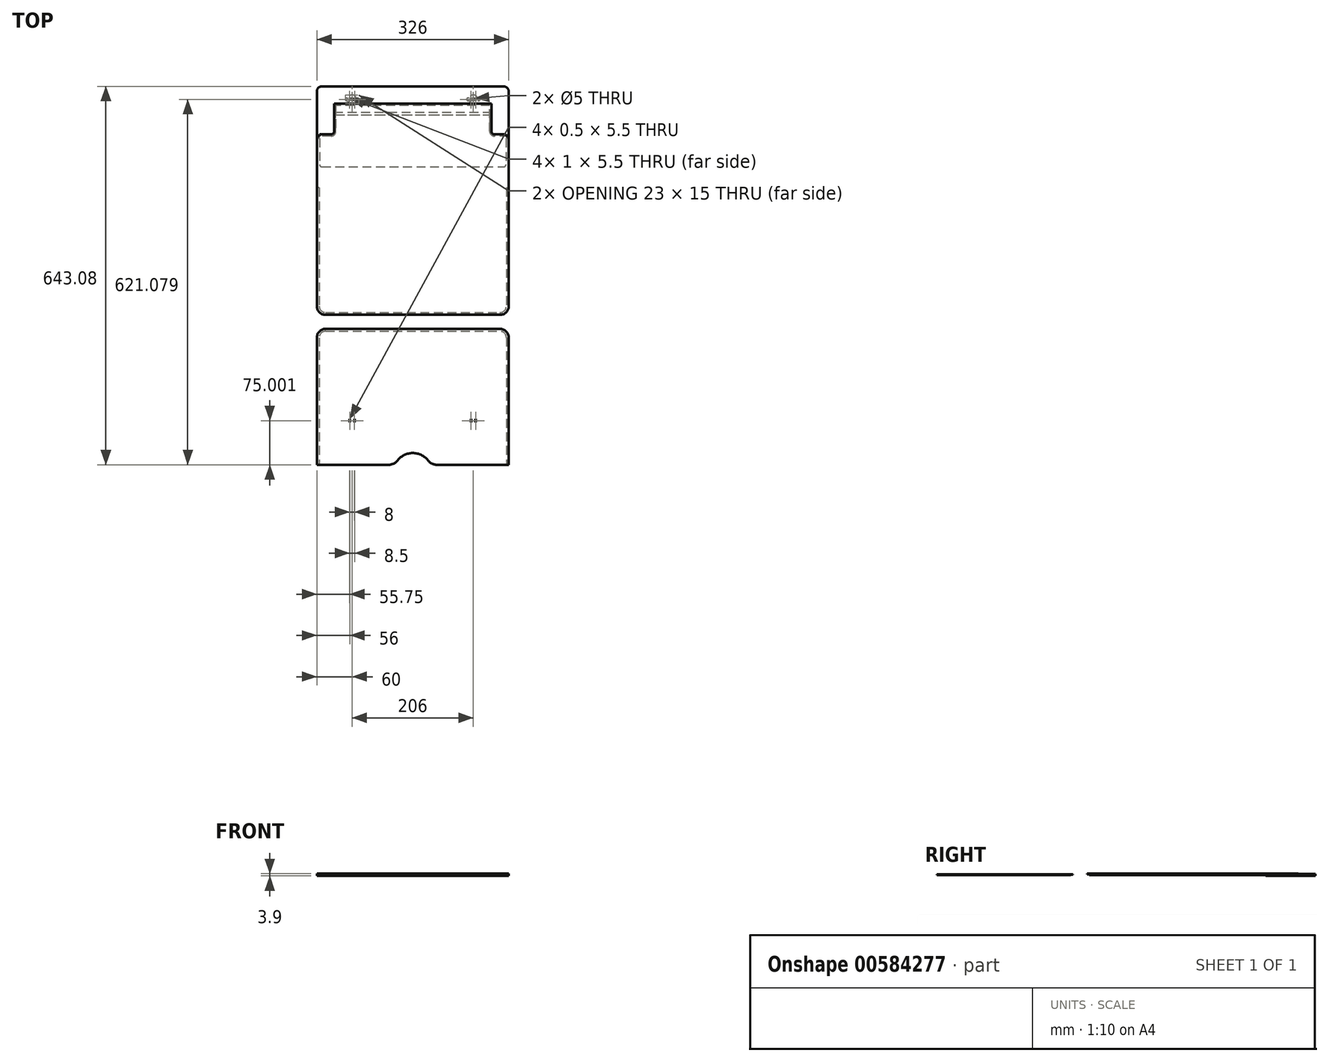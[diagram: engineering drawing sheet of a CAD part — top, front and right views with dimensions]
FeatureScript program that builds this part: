
annotation { "Feature Type Name" : "Feature", "Feature Type Description" : "" }
export const myFeature = defineFeature(function(context is Context, id is Id, definition is map)
    precondition{}
    {
        {
            var Q0;
            Q0=qCreatedBy(makeId("Top.planeOp"),FACE);
            var sketch = newSketch(context, id + "F0", { "sketchPlane" : qUnion([Q0])});
            skLineSegment(sketch, "E0.bottom", {"start": v(155, 321.54) * mm, "end": v(-155, 321.54) * mm});
            skLineSegment(sketch, "E0.top", {"start": v(-41.23, -321.54) * mm, "end": v(-163, -321.54) * mm});
            skLineSegment(sketch, "E0.left", {"start": v(163, 313.54) * mm, "end": v(163, 164.26) * mm});
            skLineSegment(sketch, "E0.right", {"start": v(-163, 313.54) * mm, "end": v(-163, 164.26) * mm});
            skPoint(sketch, "E0.middle", {"position": v(0, 0) * mm});
            skPoint(sketch, "E1", {"position": v(163, 184.96) * mm});
            skLineSegment(sketch, "E2", {"start": v(163, 237.12) * mm, "end": v(138.75, 237.12) * mm});
            skLineSegment(sketch, "E3", {"start": v(130.75, 245.12) * mm, "end": v(130.75, 289.29) * mm});
            skLineSegment(sketch, "E4", {"start": v(130.75, 289.29) * mm, "end": v(-130.75, 289.29) * mm});
            skLineSegment(sketch, "E5", {"start": v(-130.75, 289.29) * mm, "end": v(-130.75, 245.12) * mm});
            skLineSegment(sketch, "E6", {"start": v(-138.75, 237.12) * mm, "end": v(-163, 237.12) * mm});
            skLineSegment(sketch, "E7", {"start": v(-60.78, 289.29) * mm, "end": v(-60.78, 321.54) * mm, "construction": true});
            skPoint(sketch, "E8.visualSharp", {"position": v(-163, 321.54) * mm});
            skArc(sketch, "E8.filletArc", {"start": v(-155, 321.54) * mm, "mid": v(-160.66, 319.2) * mm, "end": v(-163, 313.54) * mm});
            skPoint(sketch, "E9.visualSharp", {"position": v(163, 321.54) * mm});
            skArc(sketch, "E9.filletArc", {"start": v(163, 313.54) * mm, "mid": v(160.66, 319.2) * mm, "end": v(155, 321.54) * mm});
            skPoint(sketch, "E10.visualSharp", {"position": v(130.75, 237.12) * mm});
            skArc(sketch, "E10.filletArc", {"start": v(130.75, 245.12) * mm, "mid": v(133.1, 239.46) * mm, "end": v(138.75, 237.12) * mm});
            skPoint(sketch, "E11.visualSharp", {"position": v(-130.75, 237.12) * mm});
            skArc(sketch, "E11.filletArc", {"start": v(-138.75, 237.12) * mm, "mid": v(-133.1, 239.46) * mm, "end": v(-130.75, 245.12) * mm});
            skLineSegment(sketch, "E12", {"start": v(-163, 247.5) * mm, "end": v(-130.75, 247.5) * mm, "construction": true});
            skLineSegment(sketch, "E13", {"start": v(163, 184.96) * mm, "end": v(-163, 184.96) * mm, "construction": true});
            skArc(sketch, "E14", {"start": v(25.52, -313.92) * mm, "mid": v(0, -301.54) * mm, "end": v(-25.52, -313.92) * mm});
            skPoint(sketch, "E15.newPointA", {"position": v(-30, -321.54) * mm});
            skPoint(sketch, "E15.newPointB", {"position": v(163, -321.54) * mm});
            skArc(sketch, "E15.filletArc", {"start": v(-41.23, -321.54) * mm, "mid": v(-32.5, -319.53) * mm, "end": v(-25.52, -313.92) * mm});
            skLineSegment(sketch, "E16", {"start": v(41.23, -321.54) * mm, "end": v(163, -321.54) * mm});
            skPoint(sketch, "E17.visualSharp", {"position": v(30, -321.54) * mm});
            skArc(sketch, "E17.filletArc", {"start": v(25.52, -313.92) * mm, "mid": v(32.5, -319.53) * mm, "end": v(41.23, -321.54) * mm});
            skLineSegment(sketch, "E18.0", {"start": v(-138.75, 240.12) * mm, "end": v(-158.5, 240.12) * mm});
            skArc(sketch, "E18.1", {"start": v(-138.75, 240.12) * mm, "mid": v(-135.22, 241.58) * mm, "end": v(-133.75, 245.12) * mm});
            skLineSegment(sketch, "E18.2", {"start": v(-133.75, 292.29) * mm, "end": v(-133.75, 245.12) * mm});
            skLineSegment(sketch, "E18.3", {"start": v(158.5, 240.12) * mm, "end": v(138.75, 240.12) * mm});
            skArc(sketch, "E18.4", {"start": v(133.75, 245.12) * mm, "mid": v(135.22, 241.58) * mm, "end": v(138.75, 240.12) * mm});
            skLineSegment(sketch, "E18.5", {"start": v(133.75, 245.12) * mm, "end": v(133.75, 292.29) * mm});
            skLineSegment(sketch, "E18.6", {"start": v(133.75, 292.29) * mm, "end": v(-133.75, 292.29) * mm});
            skLineSegment(sketch, "E19", {"start": v(-158.5, 240.12) * mm, "end": v(-158.5, 237.12) * mm});
            skLineSegment(sketch, "E20.MirrorCS", {"start": v(158.5, 240.12) * mm, "end": v(158.5, 237.12) * mm});
            skLineSegment(sketch, "E21", {"start": v(-148, -90.54) * mm, "end": v(148, -90.54) * mm});
            skLineSegment(sketch, "E22", {"start": v(-148, -66.74) * mm, "end": v(148, -66.74) * mm});
            skArc(sketch, "E23.filletArc", {"start": v(-163, -51.74) * mm, "mid": v(-158.6, -62.35) * mm, "end": v(-148, -66.74) * mm});
            skArc(sketch, "E24.filletArc", {"start": v(148, -66.74) * mm, "mid": v(158.6, -62.35) * mm, "end": v(163, -51.74) * mm});
            skLineSegment(sketch, "E25", {"start": v(-163, -105.54) * mm, "end": v(-163, -321.54) * mm});
            skLineSegment(sketch, "E26", {"start": v(163, -105.54) * mm, "end": v(163, -321.54) * mm});
            skPoint(sketch, "E27.visualSharp", {"position": v(-163, -90.54) * mm});
            skArc(sketch, "E27.filletArc", {"start": v(-148, -90.54) * mm, "mid": v(-158.6, -94.93) * mm, "end": v(-163, -105.54) * mm});
            skPoint(sketch, "E28.visualSharp", {"position": v(163, -90.54) * mm});
            skArc(sketch, "E28.filletArc", {"start": v(163, -105.54) * mm, "mid": v(158.6, -94.93) * mm, "end": v(148, -90.54) * mm});
            skLineSegment(sketch, "E29.bottom", {"start": v(-107.25, -243.79) * mm, "end": v(-106.75, -243.79) * mm});
            skLineSegment(sketch, "E29.top", {"start": v(-107.25, -249.29) * mm, "end": v(-106.75, -249.29) * mm});
            skLineSegment(sketch, "E29.left", {"start": v(-107.25, -243.79) * mm, "end": v(-107.25, -249.29) * mm});
            skLineSegment(sketch, "E29.right", {"start": v(-106.75, -243.79) * mm, "end": v(-106.75, -249.29) * mm});
            skLineSegment(sketch, "E30", {"start": v(-103, -250.73) * mm, "end": v(-103, -259.37) * mm, "construction": true});
            skPoint(sketch, "E31.orphan", {"position": v(-90.2, -187.28) * mm});
            skLineSegment(sketch, "E32.MirrorCS", {"start": v(-98.75, -249.29) * mm, "end": v(-99.25, -249.29) * mm});
            skLineSegment(sketch, "E33.MirrorCS", {"start": v(-99.25, -243.79) * mm, "end": v(-99.25, -249.29) * mm});
            skLineSegment(sketch, "E34.MirrorCS", {"start": v(-98.75, -243.79) * mm, "end": v(-98.75, -249.29) * mm});
            skLineSegment(sketch, "E35.MirrorCS", {"start": v(-98.75, -243.79) * mm, "end": v(-99.25, -243.79) * mm});
            skPoint(sketch, "E36", {"position": v(-103, -246.54) * mm});
            skLineSegment(sketch, "E37.trimOffspring", {"start": v(-106.75, -246.54) * mm, "end": v(-99.25, -246.54) * mm, "construction": true});
            skPoint(sketch, "E38.trimOffspring.end.orphan", {"position": v(-98.68, -246.54) * mm});
            skPoint(sketch, "E39.start.orphan", {"position": v(-107.32, -246.54) * mm});
            skLineSegment(sketch, "E40.MirrorCS", {"start": v(107.25, -249.29) * mm, "end": v(106.75, -249.29) * mm});
            skLineSegment(sketch, "E41.MirrorCS", {"start": v(107.25, -243.79) * mm, "end": v(106.75, -243.79) * mm});
            skLineSegment(sketch, "E42.MirrorCS", {"start": v(98.75, -243.79) * mm, "end": v(99.25, -243.79) * mm});
            skLineSegment(sketch, "E43.MirrorCS", {"start": v(98.75, -249.29) * mm, "end": v(99.25, -249.29) * mm});
            skPoint(sketch, "E44.MirrorP", {"position": v(107.32, -246.54) * mm});
            skLineSegment(sketch, "E45.MirrorCS", {"start": v(98.75, -243.79) * mm, "end": v(98.75, -249.29) * mm});
            skLineSegment(sketch, "E46.MirrorCS", {"start": v(106.75, -246.54) * mm, "end": v(99.25, -246.54) * mm, "construction": true});
            skLineSegment(sketch, "E47.MirrorCS", {"start": v(106.75, -243.79) * mm, "end": v(106.75, -249.29) * mm});
            skPoint(sketch, "E48.MirrorP", {"position": v(103, -246.54) * mm});
            skLineSegment(sketch, "E49.MirrorCS", {"start": v(107.25, -243.79) * mm, "end": v(107.25, -249.29) * mm});
            skLineSegment(sketch, "E50.MirrorCS", {"start": v(99.25, -243.79) * mm, "end": v(99.25, -249.29) * mm});
            skPoint(sketch, "E51.MirrorP", {"position": v(98.68, -246.54) * mm});
            skLineSegment(sketch, "E52", {"start": v(-163, 164.26) * mm, "end": v(163, 164.26) * mm, "construction": true});
            skLineSegment(sketch, "E53", {"start": v(-163, 164.26) * mm, "end": v(-163, -51.74) * mm});
            skLineSegment(sketch, "E54", {"start": v(163, 164.26) * mm, "end": v(163, -51.74) * mm});
            skSolve(sketch);
        }
        {
            var Q0;
            {var subQ1=sQuery(id+"F0.wireOp",EDGE,"E0.top");Q0=makeQuery(id+"F0.imprint","IMPRINT",FACE,{"disambiguationData":[TD([[makeQuery(id+"F0.imprint","IMPRINT",EDGE,{"derivedFrom":subQ1}),-1.0]])]});}
            extrude(context, id + "F1", {"entities" : qUnion([Q0]), "oppositeDirection" : true, "depth" : 0.8 * mm, "offsetDistance" : 25 * mm});
        }
        {
            var Q0;
            Q0=makeQuery(id+"F0.imprint","IMPRINT",FACE,{"disambiguationData":[TD([[makeQuery(id+"F0.imprint","IMPRINT",EDGE,{"derivedFrom":sQuery(id+"F0.wireOp",EDGE,"E3")}),1.0]])]});
            var Q1;
            Q1=makeQuery(id+"F0.imprint","IMPRINT",FACE,{"disambiguationData":[TD([[makeQuery(id+"F0.imprint","IMPRINT",EDGE,{"derivedFrom":sQuery(id+"F0.wireOp",EDGE,"E3")}),-1.0]])]});
            extrude(context, id + "F2", {"entities" : qUnion([Q0, Q1]), "depth" : 0.9 * mm, "offsetDistance" : 25 * mm});
        }
        {
            var Q0;
            Q0=makeQuery(id+"F0.imprint","IMPRINT",FACE,{"disambiguationData":[TD([[makeQuery(id+"F0.imprint","IMPRINT",EDGE,{"derivedFrom":sQuery(id+"F0.wireOp",EDGE,"E0.bottom")}),1.0]])]});
            extrude(context, id + "F3", {"entities" : qUnion([Q0]), "oppositeDirection" : true, "depth" : 0.9 * mm, "offsetDistance" : 25 * mm});
        }
        {
            var Q0;
            Q0=makeQuery(id+"F0.imprint","IMPRINT",FACE,{"disambiguationData":[TD([[makeQuery(id+"F0.imprint","IMPRINT",EDGE,{"derivedFrom":sQuery(id+"F0.wireOp",EDGE,"E3")}),-1.0]])]});
            var Q1;
            Q1=makeQuery(id+"F0.imprint","IMPRINT",FACE,{"disambiguationData":[TD([[makeQuery(id+"F0.imprint","IMPRINT",EDGE,{"derivedFrom":sQuery(id+"F0.wireOp",EDGE,"E0.bottom")}),1.0]])]});
            extrude(context, id + "F4", {"entities" : qUnion([Q0, Q1]), "depth" : 0.6 * mm, "offsetDistance" : 25 * mm});
        }
        {
            var Q0;
            Q0=makeQuery(id+"F3.opExtrude","CAP_FACE",FACE,{"disambiguationData":[OSD([sQuery(id+"F0.wireOp",EDGE,"E0.bottom"),sQuery(id+"F0.wireOp",EDGE,"E0.left"),sQuery(id+"F0.wireOp",EDGE,"E0.right"),sQuery(id+"F0.wireOp",EDGE,"E2"),sQuery(id+"F0.wireOp",EDGE,"E6"),sQuery(id+"F0.wireOp",EDGE,"E8.filletArc"),sQuery(id+"F0.wireOp",EDGE,"E9.filletArc"),sQuery(id+"F0.wireOp",EDGE,"E18.0"),sQuery(id+"F0.wireOp",EDGE,"E18.2"),sQuery(id+"F0.wireOp",EDGE,"E18.3"),sQuery(id+"F0.wireOp",EDGE,"E18.5"),sQuery(id+"F0.wireOp",EDGE,"E18.6"),sQuery(id+"F0.wireOp",EDGE,"E19"),sQuery(id+"F0.wireOp",EDGE,"E20.MirrorCS")])],"isStart":false});
            var sketch = newSketch(context, id + "F5", { "sketchPlane" : qUnion([Q0])});
            skLineSegment(sketch, "E55.0", {"start": v(-163, -313.54) * mm, "end": v(-163, -237.12) * mm});
            skArc(sketch, "E56.0", {"start": v(-155, -321.54) * mm, "mid": v(-160.66, -319.2) * mm, "end": v(-163, -313.54) * mm});
            skLineSegment(sketch, "E57.0", {"start": v(155, -321.54) * mm, "end": v(-155, -321.54) * mm});
            skArc(sketch, "E58.0", {"start": v(163, -313.54) * mm, "mid": v(160.66, -319.2) * mm, "end": v(155, -321.54) * mm});
            skLineSegment(sketch, "E59.0", {"start": v(163, -313.54) * mm, "end": v(163, -237.12) * mm});
            skPoint(sketch, "E60.orphan", {"position": v(-163, -164.26) * mm});
            skPoint(sketch, "E61.orphan", {"position": v(163, -164.26) * mm});
            skLineSegment(sketch, "E62.0", {"start": v(-158.5, -240.12) * mm, "end": v(-158.5, -237.12) * mm});
            skLineSegment(sketch, "E63", {"start": v(-158.5, -232.99) * mm, "end": v(-158.5, -188.96) * mm});
            skArc(sketch, "E64", {"start": v(-158.86, -233.38) * mm, "mid": v(-161.28, -234.6) * mm, "end": v(-162.25, -237.12) * mm});
            skPoint(sketch, "E65.newPointB", {"position": v(-162.25, -237.12) * mm});
            skArc(sketch, "E66.filletArc", {"start": v(-158.86, -233.38) * mm, "mid": v(-158.6, -233.26) * mm, "end": v(-158.5, -232.99) * mm});
            skLineSegment(sketch, "E67.0", {"start": v(0, -184.96) * mm, "end": v(-154.5, -184.96) * mm});
            skPoint(sketch, "E68.newPointB", {"position": v(-163, -184.96) * mm});
            skArc(sketch, "E68.filletArc", {"start": v(-154.5, -184.96) * mm, "mid": v(-157.33, -186.13) * mm, "end": v(-158.5, -188.96) * mm});
            skPoint(sketch, "E69.orphan", {"position": v(163, -184.96) * mm});
            skLineSegment(sketch, "E70.MirrorCS", {"start": v(0, -184.96) * mm, "end": v(154.5, -184.96) * mm});
            skArc(sketch, "E71.MirrorCS", {"start": v(154.5, -184.96) * mm, "mid": v(157.33, -186.13) * mm, "end": v(158.5, -188.96) * mm});
            skLineSegment(sketch, "E72.MirrorCS", {"start": v(158.5, -232.99) * mm, "end": v(158.5, -188.96) * mm});
            skArc(sketch, "E73.MirrorCS", {"start": v(158.86, -233.38) * mm, "mid": v(158.6, -233.26) * mm, "end": v(158.5, -232.99) * mm});
            skArc(sketch, "E74.MirrorCS", {"start": v(158.86, -233.38) * mm, "mid": v(161.28, -234.6) * mm, "end": v(162.25, -237.12) * mm});
            skLineSegment(sketch, "E75", {"start": v(-163, -237.12) * mm, "end": v(-162.25, -237.12) * mm});
            skLineSegment(sketch, "E76", {"start": v(162.25, -237.12) * mm, "end": v(163, -237.12) * mm});
            skSolve(sketch);
        }
        {
            var Q0;
            Q0=qSketchRegion(id+"F5",true);
            extrude(context, id + "F6", {"entities" : qUnion([Q0]), "depth" : 0.6 * mm, "offsetDistance" : 25 * mm});
        }
        {
            var Q0;
            Q0=makeQuery(id+"F6.opExtrude","CAP_FACE",FACE,{"disambiguationData":[OSD([sQuery(id+"F5.wireOp",EDGE,"E55.0"),sQuery(id+"F5.wireOp",EDGE,"E56.0"),sQuery(id+"F5.wireOp",EDGE,"E57.0"),sQuery(id+"F5.wireOp",EDGE,"E58.0"),sQuery(id+"F5.wireOp",EDGE,"E59.0"),sQuery(id+"F5.wireOp",EDGE,"mqd3fcgL-vkYM-jt8C-SEZb-QTAqxbzKtnkH"),sQuery(id+"F5.wireOp",EDGE,"E63"),sQuery(id+"F5.wireOp",EDGE,"E64"),sQuery(id+"F5.wireOp",EDGE,"E65.filletArc"),sQuery(id+"F5.wireOp",EDGE,"E66.filletArc"),sQuery(id+"F5.wireOp",EDGE,"E67.0"),sQuery(id+"F5.wireOp",EDGE,"E68.filletArc"),sQuery(id+"F5.wireOp",EDGE,"E70.MirrorCS"),sQuery(id+"F5.wireOp",EDGE,"E71.MirrorCS"),sQuery(id+"F5.wireOp",EDGE,"E72.MirrorCS"),sQuery(id+"F5.wireOp",EDGE,"E73.MirrorCS"),sQuery(id+"F5.wireOp",EDGE,"E74.MirrorCS"),sQuery(id+"F5.wireOp",EDGE,"eea31a7d-e614-436a-bde2-b2130c57034b0.MirrorCS"),sQuery(id+"F5.wireOp",EDGE,"bd1179cf-cb36-4206-b0af-3bf9bbb72a3d0.MirrorCS")])],"isStart":false});
            var sketch = newSketch(context, id + "F7", { "sketchPlane" : qUnion([Q0])});
            skLineSegment(sketch, "E77.0.0", {"start": v(-158.5, -237.12) * mm, "end": v(-158.5, -240.12) * mm});
            skLineSegment(sketch, "E77.0.1", {"start": v(-158.5, -240.12) * mm, "end": v(-138.75, -240.12) * mm});
            skArc(sketch, "E77.0.2", {"start": v(-138.75, -240.12) * mm, "mid": v(-135.22, -241.58) * mm, "end": v(-133.75, -245.12) * mm});
            skLineSegment(sketch, "E77.0.3", {"start": v(-133.75, -245.12) * mm, "end": v(-133.75, -277.54) * mm});
            skLineSegment(sketch, "E77.0.5", {"start": v(133.75, -277.54) * mm, "end": v(133.75, -245.12) * mm});
            skArc(sketch, "E77.0.6", {"start": v(133.75, -245.12) * mm, "mid": v(135.22, -241.58) * mm, "end": v(138.75, -240.12) * mm});
            skLineSegment(sketch, "E77.0.7", {"start": v(138.75, -240.12) * mm, "end": v(158.5, -240.12) * mm});
            skLineSegment(sketch, "E77.0.8", {"start": v(158.5, -240.12) * mm, "end": v(158.5, -237.12) * mm});
            skLineSegment(sketch, "E77.0.9", {"start": v(158.5, -237.12) * mm, "end": v(163, -237.12) * mm});
            skLineSegment(sketch, "E77.0.10", {"start": v(163, -237.12) * mm, "end": v(163, -313.54) * mm});
            skArc(sketch, "E77.0.11", {"start": v(163, -313.54) * mm, "mid": v(160.66, -319.2) * mm, "end": v(155, -321.54) * mm});
            skLineSegment(sketch, "E77.0.12", {"start": v(155, -321.54) * mm, "end": v(-155, -321.54) * mm});
            skArc(sketch, "E77.0.13", {"start": v(-155, -321.54) * mm, "mid": v(-160.66, -319.2) * mm, "end": v(-163, -313.54) * mm});
            skLineSegment(sketch, "E77.0.14", {"start": v(-163, -313.54) * mm, "end": v(-163, -237.12) * mm});
            skLineSegment(sketch, "E77.0.15", {"start": v(-163, -237.12) * mm, "end": v(-158.5, -237.12) * mm});
            skLineSegment(sketch, "E78", {"start": v(-133.75, -277.54) * mm, "end": v(133.75, -277.54) * mm});
            skPoint(sketch, "E77.0.4.end.orphan", {"position": v(133.75, -292.29) * mm});
            skPoint(sketch, "E77.0.4.start.orphan", {"position": v(-133.75, -292.29) * mm});
            skArc(sketch, "E79", {"start": v(-110.07, -302.04) * mm, "mid": v(-103, -307.04) * mm, "end": v(-95.93, -302.04) * mm});
            skLineSegment(sketch, "E80", {"start": v(-112, -299.54) * mm, "end": v(-94, -299.54) * mm, "construction": true});
            skLineSegment(sketch, "E81", {"start": v(-103, -292.04) * mm, "end": v(-103, -234.35) * mm, "construction": true});
            skArc(sketch, "E82.0.startCap", {"start": v(-112, -302.04) * mm, "mid": v(-114.5, -299.54) * mm, "end": v(-112, -297.04) * mm});
            skArc(sketch, "E82.0.endCap", {"start": v(-94, -297.04) * mm, "mid": v(-91.5, -299.54) * mm, "end": v(-94, -302.04) * mm});
            skLineSegment(sketch, "E82.0.left", {"start": v(-112, -297.04) * mm, "end": v(-110.07, -297.04) * mm});
            skLineSegment(sketch, "E82.0.right", {"start": v(-112, -302.04) * mm, "end": v(-110.07, -302.04) * mm});
            skLineSegment(sketch, "E83.trimOffspring", {"start": v(-95.93, -297.04) * mm, "end": v(-94, -297.04) * mm});
            skLineSegment(sketch, "E84.trimOffspring", {"start": v(-95.93, -302.04) * mm, "end": v(-94, -302.04) * mm});
            skArc(sketch, "E85.trimOffspring", {"start": v(-95.93, -297.04) * mm, "mid": v(-103, -292.04) * mm, "end": v(-110.07, -297.04) * mm});
            skArc(sketch, "E86.MirrorCS", {"start": v(110.07, -302.04) * mm, "mid": v(103, -307.04) * mm, "end": v(95.93, -302.04) * mm});
            skLineSegment(sketch, "E87.MirrorCS", {"start": v(112, -302.04) * mm, "end": v(110.07, -302.04) * mm});
            skArc(sketch, "E88.MirrorCS", {"start": v(112, -302.04) * mm, "mid": v(114.5, -299.54) * mm, "end": v(112, -297.04) * mm});
            skLineSegment(sketch, "E89.MirrorCS", {"start": v(112, -297.04) * mm, "end": v(110.07, -297.04) * mm});
            skArc(sketch, "E90.MirrorCS", {"start": v(95.93, -297.04) * mm, "mid": v(103, -292.04) * mm, "end": v(110.07, -297.04) * mm});
            skLineSegment(sketch, "E91.MirrorCS", {"start": v(95.93, -297.04) * mm, "end": v(94, -297.04) * mm});
            skArc(sketch, "E92.MirrorCS", {"start": v(94, -297.04) * mm, "mid": v(91.5, -299.54) * mm, "end": v(94, -302.04) * mm});
            skLineSegment(sketch, "E93.MirrorCS", {"start": v(95.93, -302.04) * mm, "end": v(94, -302.04) * mm});
            skSolve(sketch);
        }
        {
            var Q0;
            {var subQ1=sQuery(id+"F7.wireOp",EDGE,"E77.0.0");Q0=makeQuery(id+"F7.imprint","IMPRINT",FACE,{"disambiguationData":[TD([[makeQuery(id+"F7.imprint","IMPRINT",EDGE,{"derivedFrom":subQ1}),-1.0]])]});}
            extrude(context, id + "F8", {"entities" : qUnion([Q0]), "depth" : 0.9 * mm, "offsetDistance" : 25 * mm});
        }
        {
            var Q0;
            Q0=makeQuery(id+"F8.opExtrude","CAP_FACE",FACE,{"disambiguationData":[OSD([sQuery(id+"F5.wireOp",EDGE,"mqd3fcgL-vkYM-jt8C-SEZb-QTAqxbzKtnkH"),sQuery(id+"F5.wireOp",EDGE,"E65.filletArc"),sQuery(id+"F5.wireOp",EDGE,"eea31a7d-e614-436a-bde2-b2130c57034b0.MirrorCS"),sQuery(id+"F5.wireOp",EDGE,"bd1179cf-cb36-4206-b0af-3bf9bbb72a3d0.MirrorCS"),sQuery(id+"F7.wireOp",EDGE,"E77.0.0"),sQuery(id+"F7.wireOp",EDGE,"E77.0.1"),sQuery(id+"F7.wireOp",EDGE,"E77.0.2"),sQuery(id+"F7.wireOp",EDGE,"E77.0.3"),sQuery(id+"F7.wireOp",EDGE,"E77.0.5"),sQuery(id+"F7.wireOp",EDGE,"E77.0.6"),sQuery(id+"F7.wireOp",EDGE,"E77.0.7"),sQuery(id+"F7.wireOp",EDGE,"E77.0.8"),sQuery(id+"F7.wireOp",EDGE,"E77.0.9"),sQuery(id+"F7.wireOp",EDGE,"E77.0.10"),sQuery(id+"F7.wireOp",EDGE,"E77.0.11"),sQuery(id+"F7.wireOp",EDGE,"E77.0.12"),sQuery(id+"F7.wireOp",EDGE,"E77.0.13"),sQuery(id+"F7.wireOp",EDGE,"E77.0.14"),sQuery(id+"F7.wireOp",EDGE,"E77.0.15"),sQuery(id+"F7.wireOp",EDGE,"E78"),sQuery(id+"F7.wireOp",EDGE,"E79"),sQuery(id+"F7.wireOp",EDGE,"E82.0.startCap"),sQuery(id+"F7.wireOp",EDGE,"E82.0.endCap"),sQuery(id+"F7.wireOp",EDGE,"E82.0.left"),sQuery(id+"F7.wireOp",EDGE,"E82.0.right"),sQuery(id+"F7.wireOp",EDGE,"E83.trimOffspring"),sQuery(id+"F7.wireOp",EDGE,"E84.trimOffspring"),sQuery(id+"F7.wireOp",EDGE,"E85.trimOffspring"),sQuery(id+"F7.wireOp",EDGE,"E86.MirrorCS"),sQuery(id+"F7.wireOp",EDGE,"E87.MirrorCS"),sQuery(id+"F7.wireOp",EDGE,"E88.MirrorCS"),sQuery(id+"F7.wireOp",EDGE,"E89.MirrorCS"),sQuery(id+"F7.wireOp",EDGE,"E90.MirrorCS"),sQuery(id+"F7.wireOp",EDGE,"E91.MirrorCS"),sQuery(id+"F7.wireOp",EDGE,"E92.MirrorCS"),sQuery(id+"F7.wireOp",EDGE,"E93.MirrorCS")])],"isStart":false});
            var sketch = newSketch(context, id + "F9", { "sketchPlane" : qUnion([Q0])});
            skLineSegment(sketch, "E94.0.0", {"start": v(-163, -313.54) * mm, "end": v(-163, -237.12) * mm});
            skLineSegment(sketch, "E94.0.1", {"start": v(-163, -237.12) * mm, "end": v(-138.75, -237.12) * mm});
            skArc(sketch, "E94.0.2", {"start": v(-138.75, -237.12) * mm, "mid": v(-133.1, -239.46) * mm, "end": v(-130.75, -245.12) * mm});
            skLineSegment(sketch, "E94.0.3", {"start": v(-130.75, -245.12) * mm, "end": v(-130.75, -273.54) * mm});
            skLineSegment(sketch, "E94.0.5", {"start": v(130.75, -273.54) * mm, "end": v(130.75, -245.12) * mm});
            skArc(sketch, "E94.0.6", {"start": v(130.75, -245.12) * mm, "mid": v(133.1, -239.46) * mm, "end": v(138.75, -237.12) * mm});
            skLineSegment(sketch, "E94.0.7", {"start": v(138.75, -237.12) * mm, "end": v(163, -237.12) * mm});
            skLineSegment(sketch, "E94.0.8", {"start": v(163, -237.12) * mm, "end": v(163, -313.54) * mm});
            skArc(sketch, "E94.0.9", {"start": v(163, -313.54) * mm, "mid": v(160.66, -319.2) * mm, "end": v(155, -321.54) * mm});
            skLineSegment(sketch, "E94.0.10", {"start": v(155, -321.54) * mm, "end": v(-155, -321.54) * mm});
            skArc(sketch, "E94.0.11", {"start": v(-155, -321.54) * mm, "mid": v(-160.66, -319.2) * mm, "end": v(-163, -313.54) * mm});
            skLineSegment(sketch, "E95", {"start": v(-130.75, -273.54) * mm, "end": v(130.75, -273.54) * mm});
            skPoint(sketch, "E95.startSnap0", {"position": v(-110.7, -273.54) * mm});
            skPoint(sketch, "E94.0.4.end.orphan", {"position": v(130.75, -289.29) * mm});
            skPoint(sketch, "E94.0.4.start.orphan", {"position": v(-130.75, -289.29) * mm});
            skArc(sketch, "E96.0", {"start": v(-95.93, -297.04) * mm, "mid": v(-103, -292.04) * mm, "end": v(-110.07, -297.04) * mm, "construction": true});
            skCircle(sketch, "E97", {"center": v(-103, -299.54) * mm, "radius": 2.5 * mm});
            skLineSegment(sketch, "E98.bottom", {"start": v(-107.75, -296.79) * mm, "end": v(-106.75, -296.79) * mm});
            skLineSegment(sketch, "E98.top", {"start": v(-107.75, -302.29) * mm, "end": v(-106.75, -302.29) * mm});
            skLineSegment(sketch, "E98.left", {"start": v(-107.75, -296.79) * mm, "end": v(-107.75, -302.29) * mm});
            skLineSegment(sketch, "E98.right", {"start": v(-106.75, -296.79) * mm, "end": v(-106.75, -302.29) * mm});
            skLineSegment(sketch, "E99", {"start": v(-103, -299.54) * mm, "end": v(-103, -292.04) * mm, "construction": true});
            skLineSegment(sketch, "E100.MirrorCS", {"start": v(-98.25, -302.29) * mm, "end": v(-99.25, -302.29) * mm});
            skLineSegment(sketch, "E101.MirrorCS", {"start": v(-98.25, -296.79) * mm, "end": v(-98.25, -302.29) * mm});
            skLineSegment(sketch, "E102.MirrorCS", {"start": v(-99.25, -296.79) * mm, "end": v(-99.25, -302.29) * mm});
            skLineSegment(sketch, "E103.MirrorCS", {"start": v(-98.25, -296.79) * mm, "end": v(-99.25, -296.79) * mm});
            skLineSegment(sketch, "E104", {"start": v(-105.5, -299.54) * mm, "end": v(-100.5, -299.54) * mm, "construction": true});
            skLineSegment(sketch, "E105.MirrorCS", {"start": v(107.75, -296.79) * mm, "end": v(106.75, -296.79) * mm});
            skLineSegment(sketch, "E106.MirrorCS", {"start": v(98.25, -302.29) * mm, "end": v(99.25, -302.29) * mm});
            skLineSegment(sketch, "E107.MirrorCS", {"start": v(98.25, -296.79) * mm, "end": v(99.25, -296.79) * mm});
            skLineSegment(sketch, "E108.MirrorCS", {"start": v(107.75, -302.29) * mm, "end": v(106.75, -302.29) * mm});
            skLineSegment(sketch, "E109.MirrorCS", {"start": v(98.25, -296.79) * mm, "end": v(98.25, -302.29) * mm});
            skLineSegment(sketch, "E110.MirrorCS", {"start": v(105.5, -299.54) * mm, "end": v(100.5, -299.54) * mm, "construction": true});
            skLineSegment(sketch, "E111.MirrorCS", {"start": v(107.75, -296.79) * mm, "end": v(107.75, -302.29) * mm});
            skLineSegment(sketch, "E112.MirrorCS", {"start": v(106.75, -296.79) * mm, "end": v(106.75, -302.29) * mm});
            skCircle(sketch, "E113.MirrorC", {"center": v(103, -299.54) * mm, "radius": 2.5 * mm});
            skLineSegment(sketch, "E114.MirrorCS", {"start": v(99.25, -296.79) * mm, "end": v(99.25, -302.29) * mm});
            skSolve(sketch);
        }
        {
            var Q0;
            Q0=qSketchRegion(id+"F9",true);
            extrude(context, id + "F10", {"entities" : qUnion([Q0]), "depth" : 0.6 * mm, "offsetDistance" : 25 * mm});
        }
        {
            var Q0;
            Q0=makeQuery(id+"F1.opExtrude","CAP_FACE",FACE,{"disambiguationData":[OSD([sQuery(id+"F0.wireOp",EDGE,"E0.top"),sQuery(id+"F0.wireOp",EDGE,"E0.left"),sQuery(id+"F0.wireOp",EDGE,"E0.right"),sQuery(id+"F0.wireOp",EDGE,"E14"),sQuery(id+"F0.wireOp",EDGE,"E15.filletArc"),sQuery(id+"F0.wireOp",EDGE,"E16"),sQuery(id+"F0.wireOp",EDGE,"E17.filletArc"),sQuery(id+"F0.wireOp",EDGE,"E21")])],"isStart":false});
            var sketch = newSketch(context, id + "F11", { "sketchPlane" : qUnion([Q0])});
            skLineSegment(sketch, "E115.0.2", {"start": v(159, 321.54) * mm, "end": v(41.23, 321.54) * mm});
            skArc(sketch, "E115.0.3", {"start": v(41.23, 321.54) * mm, "mid": v(32.5, 319.53) * mm, "end": v(25.52, 313.92) * mm});
            skArc(sketch, "E115.0.4", {"start": v(25.52, 313.92) * mm, "mid": v(0, 301.54) * mm, "end": v(-25.52, 313.92) * mm});
            skArc(sketch, "E115.0.5", {"start": v(-25.52, 313.92) * mm, "mid": v(-32.5, 319.53) * mm, "end": v(-41.23, 321.54) * mm});
            skLineSegment(sketch, "E115.0.6", {"start": v(-41.23, 321.54) * mm, "end": v(-159, 321.54) * mm});
            skLineSegment(sketch, "E116.0.0", {"start": v(163, -237.12) * mm, "end": v(158.5, -237.12) * mm});
            skLineSegment(sketch, "E116.0.1", {"start": v(158.5, -237.12) * mm, "end": v(158.5, -240.12) * mm});
            skLineSegment(sketch, "E116.0.2", {"start": v(158.5, -240.12) * mm, "end": v(138.75, -240.12) * mm});
            skArc(sketch, "E116.0.3", {"start": v(138.75, -240.12) * mm, "mid": v(135.22, -241.58) * mm, "end": v(133.75, -245.12) * mm});
            skLineSegment(sketch, "E116.0.4", {"start": v(133.75, -245.12) * mm, "end": v(133.75, -273.54) * mm});
            skLineSegment(sketch, "E116.0.6", {"start": v(-133.75, -273.54) * mm, "end": v(-133.75, -245.12) * mm});
            skArc(sketch, "E116.0.7", {"start": v(-133.75, -245.12) * mm, "mid": v(-135.22, -241.58) * mm, "end": v(-138.75, -240.12) * mm});
            skLineSegment(sketch, "E116.0.8", {"start": v(-138.75, -240.12) * mm, "end": v(-158.5, -240.12) * mm});
            skLineSegment(sketch, "E116.0.9", {"start": v(-158.5, -240.12) * mm, "end": v(-158.5, -237.12) * mm});
            skLineSegment(sketch, "E116.0.10", {"start": v(-158.5, -237.12) * mm, "end": v(-163, -237.12) * mm});
            skLineSegment(sketch, "E116.0.11", {"start": v(-163, -237.12) * mm, "end": v(-163, -149.26) * mm});
            skLineSegment(sketch, "E116.0.13", {"start": v(163, -149.26) * mm, "end": v(163, -237.12) * mm});
            skLineSegment(sketch, "E117", {"start": v(-159, -149.26) * mm, "end": v(-163, -149.26) * mm});
            skLineSegment(sketch, "E118.MirrorCS", {"start": v(159, -149.26) * mm, "end": v(163, -149.26) * mm});
            skPoint(sketch, "E115.0.7.start.orphan", {"position": v(-41.23, 321.54) * mm});
            skPoint(sketch, "E115.0.1.end.orphan", {"position": v(132.5, 321.54) * mm});
            skPoint(sketch, "E119.orphan", {"position": v(-148, 90.54) * mm});
            skPoint(sketch, "E120.orphan", {"position": v(148, 66.74) * mm});
            skLineSegment(sketch, "E121.0", {"start": v(159, -240.12) * mm, "end": v(159, -236.93) * mm});
            skLineSegment(sketch, "E121.1", {"start": v(-159, -149.26) * mm, "end": v(-159, 51.74) * mm});
            skArc(sketch, "E121.2", {"start": v(-159, 51.74) * mm, "mid": v(-155.78, 59.52) * mm, "end": v(-148, 62.74) * mm});
            skLineSegment(sketch, "E121.3", {"start": v(-148, 62.74) * mm, "end": v(148, 62.74) * mm});
            skArc(sketch, "E121.4", {"start": v(148, 62.74) * mm, "mid": v(155.78, 59.52) * mm, "end": v(159, 51.74) * mm});
            skLineSegment(sketch, "E122.trimOffspring", {"start": v(159, -149.26) * mm, "end": v(159, 51.74) * mm});
            skPoint(sketch, "E123.orphan", {"position": v(-163, -237.12) * mm});
            skLineSegment(sketch, "E124.0", {"start": v(-159, 105.54) * mm, "end": v(-159, 321.54) * mm});
            skLineSegment(sketch, "E124.1", {"start": v(159, 105.54) * mm, "end": v(159, 321.54) * mm});
            skArc(sketch, "E124.2", {"start": v(159, 105.54) * mm, "mid": v(155.78, 97.76) * mm, "end": v(148, 94.54) * mm});
            skLineSegment(sketch, "E124.3", {"start": v(-148, 94.54) * mm, "end": v(148, 94.54) * mm});
            skArc(sketch, "E124.4", {"start": v(-148, 94.54) * mm, "mid": v(-155.78, 97.76) * mm, "end": v(-159, 105.54) * mm});
            skLineSegment(sketch, "E125.0", {"start": v(-133.75, -273.54) * mm, "end": v(133.75, -273.54) * mm});
            skPoint(sketch, "E126.orphan", {"position": v(130.75, -273.54) * mm});
            skPoint(sketch, "E127.orphan", {"position": v(-130.75, -273.54) * mm});
            skPoint(sketch, "E116.0.5.end.orphan", {"position": v(-133.75, -292.29) * mm});
            skPoint(sketch, "E128.orphan", {"position": v(133.75, -292.29) * mm});
            skSolve(sketch);
        }
        {
            var Q0;
            Q0=qSketchRegion(id+"F11",true);
            extrude(context, id + "F12", {"entities" : qUnion([Q0]), "depth" : 0.6 * mm, "offsetDistance" : 25 * mm});
        }
    });
